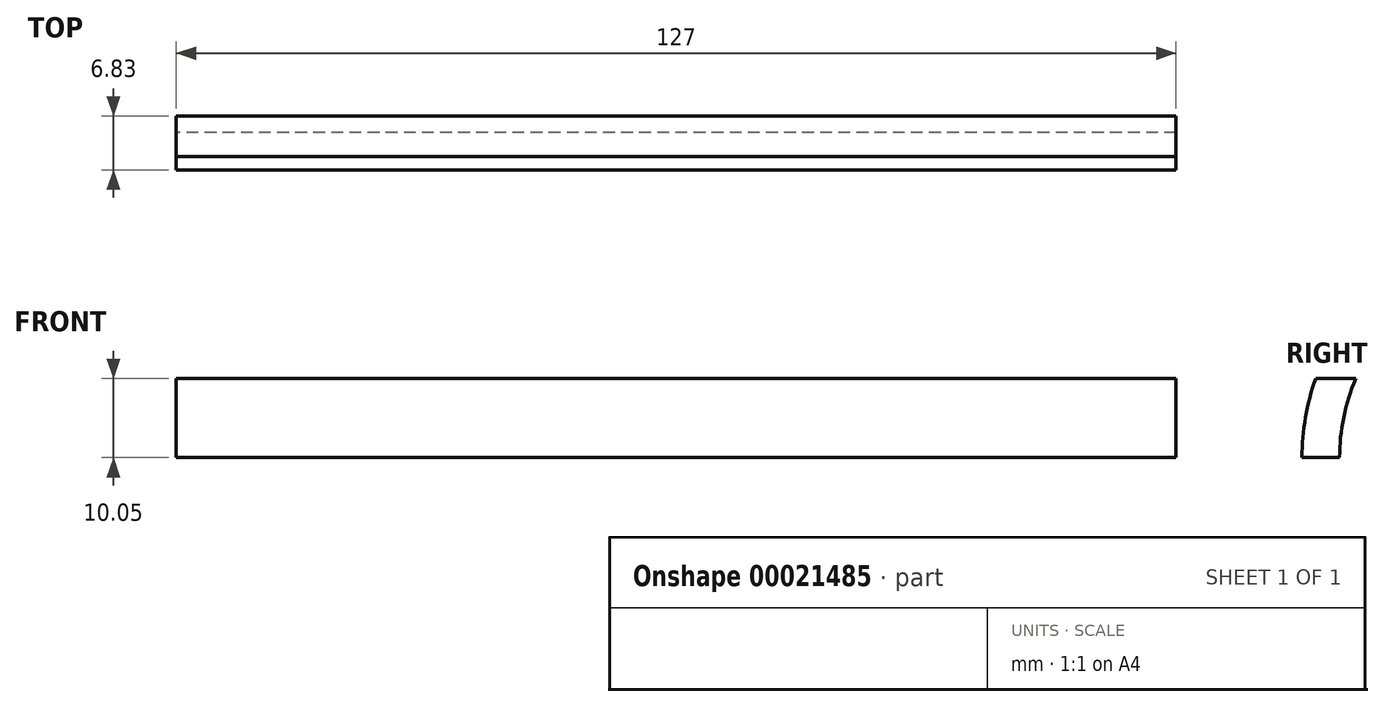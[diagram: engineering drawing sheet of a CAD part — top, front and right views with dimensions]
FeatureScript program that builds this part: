
annotation { "Feature Type Name" : "Feature", "Feature Type Description" : "" }
export const myFeature = defineFeature(function(context is Context, id is Id, definition is map)
    precondition{}
    {
        {
            var Q0;
            Q0=qCreatedBy(makeId("Right.planeOp"),FACE);
            var sketch = newSketch(context, id + "F0", { "sketchPlane" : qUnion([Q0])});
            skLineSegment(sketch, "E0", {"start": v(30.16, 0) * mm, "end": v(-30.16, 0) * mm});
            skArc(sketch, "E1", {"start": v(-30.16, 0) * mm, "mid": v(0, -30.16) * mm, "end": v(30.16, 0) * mm});
            skLineSegment(sketch, "E2", {"start": v(25.4, 0) * mm, "end": v(-25.4, 0) * mm});
            skArc(sketch, "E3", {"start": v(-25.4, 0) * mm, "mid": v(0, -25.4) * mm, "end": v(25.4, 0) * mm});
            skCircle(sketch, "E4", {"center": v(0, 0) * mm, "radius": 30.16 * mm});
            skCircle(sketch, "E5", {"center": v(0, 0) * mm, "radius": 25.4 * mm});
            skLineSegment(sketch, "E6", {"start": v(0, 30.16) * mm, "end": v(0, 10.05) * mm});
            skLineSegment(sketch, "E7", {"start": v(0, 10.05) * mm, "end": v(28.44, 10.05) * mm});
            skLineSegment(sketch, "E8", {"start": v(0, 10.05) * mm, "end": v(-23.33, 10.05) * mm});
            skLineSegment(sketch, "E9", {"start": v(-23.33, 10.05) * mm, "end": v(-28.44, 10.05) * mm});
            skSolve(sketch);
        }
        {
            var Q0;
            {var subQ0=sQuery(id+"F0.wireOp",EDGE,"E9");Q0=makeQuery(id+"F0.imprint","IMPRINT",FACE,{"disambiguationData":[TD([[makeQuery(id+"F0.imprint","IMPRINT",EDGE,{"derivedFrom":subQ0}),1.0]])]});}
            var Q1;
            {var subQ1=sQuery(id+"F0.wireOp",EDGE,"E0");var subQ5=sQuery(id+"F0.wireOp",EDGE,"E4");var subQ7=makeQuery(id+"F0.imprint","INTERSECT",VERTEX,{"disambiguationData":[OD(0.0)],"derivedFrom":[subQ1,subQ5]});Q1=makeQuery(id+"F0.imprint","IMPRINT",FACE,{"disambiguationData":[TD([[makeQuery(id+"F0.imprint","IMPRINT",EDGE,{"disambiguationData":[TD([[subQ7,1.0]])],"derivedFrom":subQ5}),1.0]])]});}
            var Q2;
            {var subQ3=sQuery(id+"F0.wireOp",EDGE,"E4");var subQ5=sQuery(id+"F0.wireOp",EDGE,"E0");var subQ7=makeQuery(id+"F0.imprint","INTERSECT",VERTEX,{"disambiguationData":[OD(0.0)],"derivedFrom":[subQ5,subQ3]});Q2=makeQuery(id+"F0.imprint","IMPRINT",FACE,{"disambiguationData":[TD([[makeQuery(id+"F0.imprint","IMPRINT",EDGE,{"disambiguationData":[TD([[subQ7,-1.0]])],"derivedFrom":subQ3}),1.0]])]});}
            extrude(context, id + "F1", {"entities" : qUnion([Q0, Q1, Q2]), "depth" : 127 * mm});
        }
        {
            var Q0;
            Q0=qCreatedBy(makeId("Top.planeOp"),FACE);
            var sketch = newSketch(context, id + "F2", { "sketchPlane" : qUnion([Q0])});
            skPoint(sketch, "E10", {"position": v(63.5, 0) * mm});
            skSolve(sketch);
        }
        {
            var Q0;
            Q0=sQuery(id+"F2.wireOp",VERTEX,"E10");
            var Q1;
            Q1=makeQuery(id+"F1.opExtrude","SWEPT_BODY",BODY,{"disambiguationData":[OSD([sQuery(id+"F0.wireOp",EDGE,"E4"),sQuery(id+"F0.wireOp",EDGE,"E5"),sQuery(id+"F0.wireOp",EDGE,"E7"),sQuery(id+"F0.wireOp",EDGE,"E9")])]});
            hole(context, id + "F3", {"style" : HoleStyle.SIMPLE, "holeDiameter" : 1.59 * mm, "endStyle" : HoleEndStyle.THROUGH, "locations" : qUnion([Q0]), "scope" : qUnion([Q1])});
        }
    });
